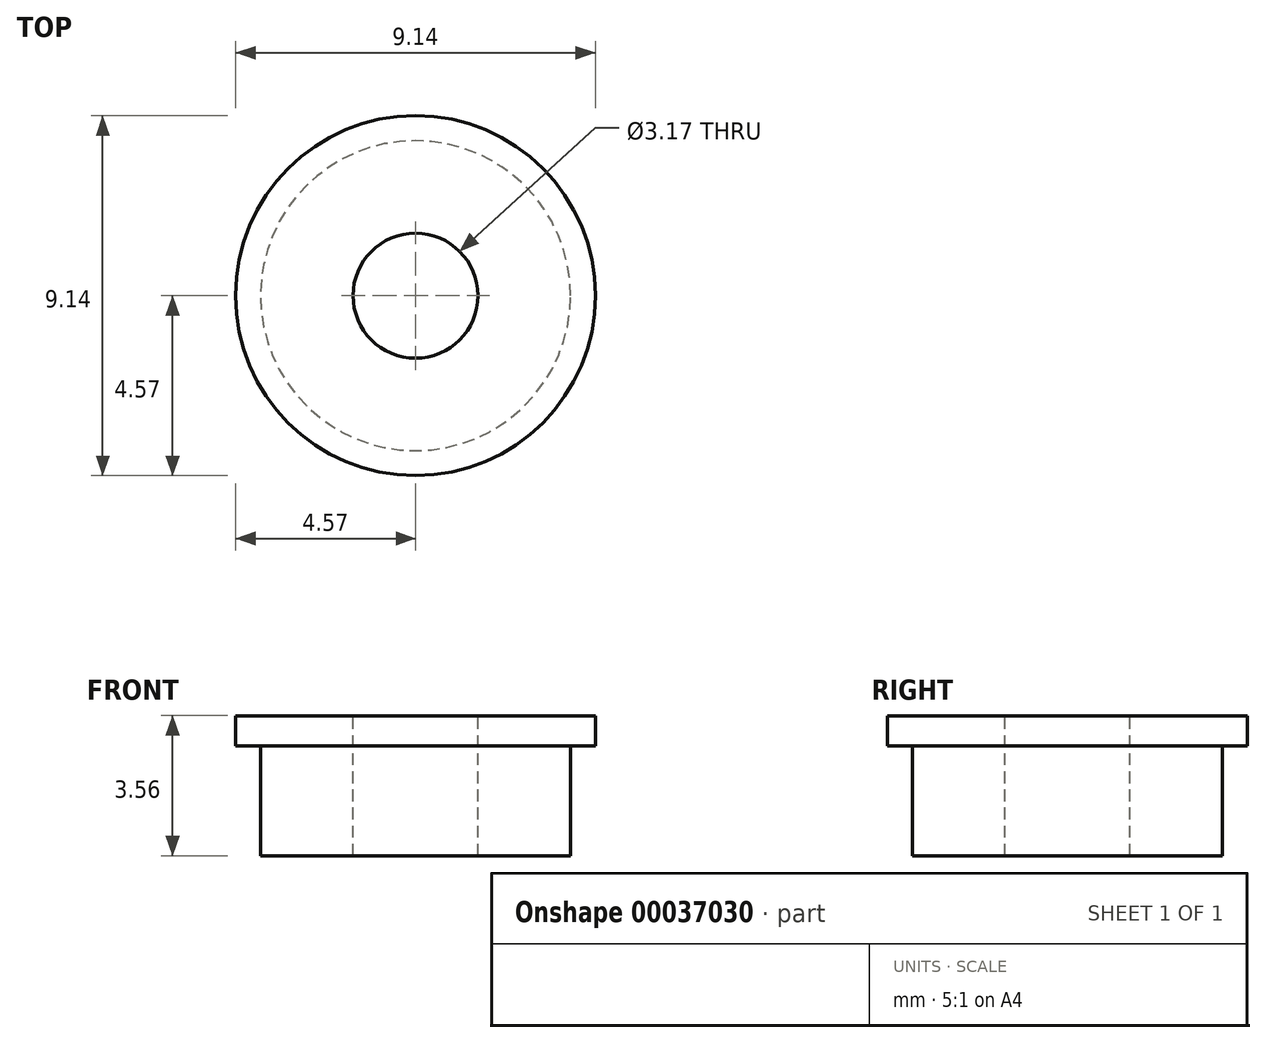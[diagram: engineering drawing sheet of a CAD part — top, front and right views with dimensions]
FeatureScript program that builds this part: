
annotation { "Feature Type Name" : "Feature", "Feature Type Description" : "" }
export const myFeature = defineFeature(function(context is Context, id is Id, definition is map)
    precondition{}
    {
        {
            var Q0;
            Q0=qCreatedBy(makeId("Front.planeOp"),FACE);
            var sketch = newSketch(context, id + "F0", { "sketchPlane" : qUnion([Q0])});
            skLineSegment(sketch, "E0", {"start": v(0, 1.78) * mm, "end": v(0, -1.78) * mm, "construction": true});
            skLineSegment(sketch, "E1", {"start": v(1.59, -1.78) * mm, "end": v(1.59, 1.78) * mm});
            skLineSegment(sketch, "E2", {"start": v(1.59, 1.78) * mm, "end": v(4.57, 1.78) * mm});
            skLineSegment(sketch, "E3", {"start": v(4.57, 1.78) * mm, "end": v(4.57, 1.02) * mm});
            skLineSegment(sketch, "E4", {"start": v(4.57, 1.02) * mm, "end": v(3.94, 1.02) * mm});
            skLineSegment(sketch, "E5", {"start": v(3.94, 1.02) * mm, "end": v(3.94, -1.78) * mm});
            skLineSegment(sketch, "E6", {"start": v(3.94, -1.78) * mm, "end": v(1.59, -1.78) * mm});
            skLineSegment(sketch, "E7", {"start": v(0, 1.78) * mm, "end": v(1.59, 1.78) * mm, "construction": true});
            skLineSegment(sketch, "E8", {"start": v(0, -1.78) * mm, "end": v(1.59, -1.78) * mm, "construction": true});
            skSolve(sketch);
        }
        {
            var Q0;
            Q0=qSketchRegion(id+"F0",true);
            var Q1;
            Q1=sQuery(id+"F0.wireOp",EDGE,"E0");
            revolve(context, id + "F1", {"entities" : qUnion([Q0]), "axis" : qUnion([Q1]), "revolveType" : RevolveType.FULL});
        }
    });
